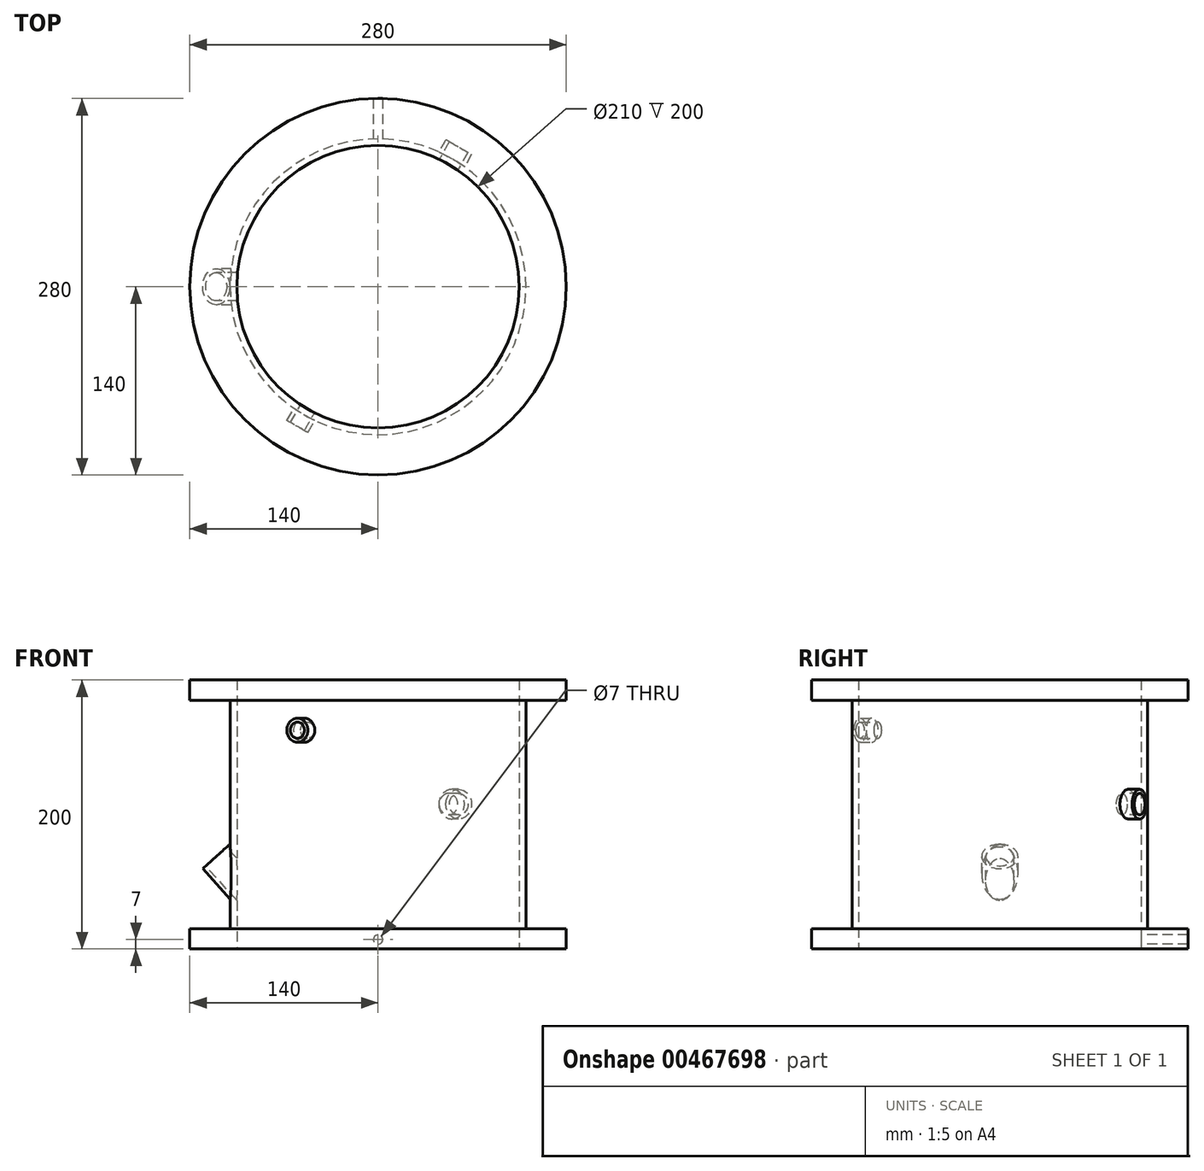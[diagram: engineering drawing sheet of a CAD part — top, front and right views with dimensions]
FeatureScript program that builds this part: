
annotation { "Feature Type Name" : "Feature", "Feature Type Description" : "" }
export const myFeature = defineFeature(function(context is Context, id is Id, definition is map)
    precondition{}
    {
        {
            var Q0;
            Q0=qCreatedBy(makeId("Front.planeOp"),FACE);
            var sketch = newSketch(context, id + "F0", { "sketchPlane" : qUnion([Q0])});
            skLineSegment(sketch, "E0", {"start": v(0, 0) * mm, "end": v(105, 0) * mm, "construction": true});
            skLineSegment(sketch, "E1", {"start": v(105, 0) * mm, "end": v(140, 0) * mm});
            skLineSegment(sketch, "E2", {"start": v(140, 0) * mm, "end": v(140, 15) * mm});
            skLineSegment(sketch, "E3", {"start": v(140, 15) * mm, "end": v(110, 15) * mm});
            skLineSegment(sketch, "E4", {"start": v(110, 15) * mm, "end": v(110, 185) * mm});
            skLineSegment(sketch, "E5", {"start": v(110, 185) * mm, "end": v(140, 185) * mm});
            skLineSegment(sketch, "E6", {"start": v(140, 185) * mm, "end": v(140, 200) * mm});
            skLineSegment(sketch, "E7", {"start": v(140, 200) * mm, "end": v(105, 200) * mm});
            skLineSegment(sketch, "E8", {"start": v(105, 200) * mm, "end": v(105, 0) * mm});
            skLineSegment(sketch, "E9", {"start": v(140, 185) * mm, "end": v(140, 15) * mm, "construction": true});
            skLineSegment(sketch, "E10", {"start": v(0, 0) * mm, "end": v(0, 197.7) * mm, "construction": true});
            skLineSegment(sketch, "E11.bottom", {"start": v(105, 200) * mm, "end": v(85, 200) * mm});
            skLineSegment(sketch, "E11.top", {"start": v(105, 0) * mm, "end": v(85, 0) * mm});
            skLineSegment(sketch, "E11.right", {"start": v(85, 200) * mm, "end": v(85, 0) * mm});
            skSolve(sketch);
        }
        {
            var Q0;
            Q0=makeQuery(id+"F0.imprint","IMPRINT",FACE,{"disambiguationData":[TD([[makeQuery(id+"F0.imprint","IMPRINT",EDGE,{"derivedFrom":sQuery(id+"F0.wireOp",EDGE,"E1")}),1.0]])]});
            var Q1;
            Q1=sQuery(id+"F0.wireOp",EDGE,"E10");
            revolve(context, id + "F1", {"entities" : qUnion([Q0]), "axis" : qUnion([Q1]), "revolveType" : RevolveType.FULL});
        }
        {
            var Q0;
            Q0=qCreatedBy(makeId("Front.planeOp"),FACE);
            var sketch = newSketch(context, id + "F2", { "sketchPlane" : qUnion([Q0])});
            skCircle(sketch, "E12", {"center": v(0, 7) * mm, "radius": 3.5 * mm});
            skSolve(sketch);
        }
        {
            var Q0;
            Q0 = qSketchRegion(id + "F2", true);
            extrude(context, id + "F3", {"entities" : qUnion([Q0]), "operationType" : NewBodyOperationType.REMOVE, "depth" : 150 * mm, "offsetDistance" : 25 * mm});
        }
        {
            var Q0;
            Q0=qCreatedBy(makeId("Front.planeOp"),FACE);
            var sketch = newSketch(context, id + "F4", { "sketchPlane" : qUnion([Q0])});
            skLineSegment(sketch, "E13", {"start": v(0, 77.7) * mm, "end": v(0, 60.53) * mm});
            skLineSegment(sketch, "E14", {"start": v(0, 77.7) * mm, "end": v(-105, 77.7) * mm});
            skLineSegment(sketch, "E15", {"start": v(-105, 77.7) * mm, "end": v(-105, 51.7) * mm});
            skLineSegment(sketch, "E16", {"start": v(-105, 51.7) * mm, "end": v(-120.4, 68.8) * mm});
            skLineSegment(sketch, "E17", {"start": v(-105, 51.7) * mm, "end": v(-105, 49.7) * mm});
            skLineSegment(sketch, "E18", {"start": v(-120.4, 68.8) * mm, "end": v(-110.36, 77.84) * mm});
            skSolve(sketch);
        }
        {
            var Q0;
            Q0=sQuery(id+"F4.wireOp",EDGE,"E18");
            cPlane(context, id + "F5", {"entities" : qUnion([Q0]), "cplaneType" : CPlaneType.LINE_ANGLE, "offset" : 25 * mm, "angle" : 90 * degree, "width" : 150 * mm, "height" : 150 * mm});
        }
        {
            var Q0;
            Q0=qCreatedBy(id+"F5.planeOp",FACE);
            var sketch = newSketch(context, id + "F6", { "sketchPlane" : qUnion([Q0])});
            skCircle(sketch, "E19", {"center": v(-43.43, 0) * mm, "radius": 13.5 * mm});
            skCircle(sketch, "E20.0", {"center": v(-43.43, 0) * mm, "radius": 10.5 * mm});
            skSolve(sketch);
        }
        {
            var Q0;
            Q0=makeQuery(id+"F6.imprint","IMPRINT",FACE,{"disambiguationData":[TD([[makeQuery(id+"F6.imprint","IMPRINT",EDGE,{"derivedFrom":sQuery(id+"F6.wireOp",EDGE,"E19")}),1.0]])]});
            extrude(context, id + "F7", {"entities" : qUnion([Q0]), "operationType" : NewBodyOperationType.ADD, "oppositeDirection" : true, "depth" : 31 * mm});
        }
        {
            var Q0;
            Q0=makeQuery(id+"F0.imprint","IMPRINT",FACE,{"disambiguationData":[TD([[makeQuery(id+"F0.imprint","IMPRINT",EDGE,{"derivedFrom":sQuery(id+"F0.wireOp",EDGE,"E11.bottom")}),1.0]])]});
            var Q1;
            Q1=sQuery(id+"F0.wireOp",EDGE,"E10");
            revolve(context, id + "F8", {"operationType" : NewBodyOperationType.REMOVE, "entities" : qUnion([Q0]), "axis" : qUnion([Q1]), "revolveType" : RevolveType.FULL, "oppositeDirection" : true});
        }
        {
            var Q0;
            Q0=qCreatedBy(makeId("Top.planeOp"),FACE);
            var sketch = newSketch(context, id + "F9", { "sketchPlane" : qUnion([Q0])});
            skLineSegment(sketch, "E21", {"start": v(0, 0) * mm, "end": v(-24.71, 42.8) * mm});
            skLineSegment(sketch, "E22", {"start": v(0, 0) * mm, "end": v(0, 44.2) * mm});
            skSolve(sketch);
        }
        {
            var Q0;
            Q0=sQuery(id+"F9.wireOp",EDGE,"E21");
            cPlane(context, id + "F10", {"entities" : qUnion([Q0]), "cplaneType" : CPlaneType.LINE_ANGLE, "offset" : 25 * mm, "angle" : 90 * degree, "width" : 150 * mm, "height" : 150 * mm});
        }
        {
            var Q0;
            Q0=qCreatedBy(id+"F10.planeOp",FACE);
            var sketch = newSketch(context, id + "F11", { "sketchPlane" : qUnion([Q0])});
            skLineSegment(sketch, "E23", {"start": v(0, 162.7) * mm, "end": v(105, 162.7) * mm});
            skLineSegment(sketch, "E24", {"start": v(105, 162.7) * mm, "end": v(120, 162.7) * mm});
            skLineSegment(sketch, "E25", {"start": v(0, 107.7) * mm, "end": v(-105, 107.7) * mm});
            skLineSegment(sketch, "E26", {"start": v(-105, 107.7) * mm, "end": v(-120, 107.7) * mm});
            skLineSegment(sketch, "E27", {"start": v(-105, 107.7) * mm, "end": v(-105, 118.7) * mm});
            skLineSegment(sketch, "E28", {"start": v(-105, 118.7) * mm, "end": v(-120, 118.7) * mm});
            skLineSegment(sketch, "E29", {"start": v(-120, 118.7) * mm, "end": v(-120, 115.7) * mm});
            skLineSegment(sketch, "E30", {"start": v(-120, 115.7) * mm, "end": v(-105, 115.7) * mm});
            skLineSegment(sketch, "E31", {"start": v(105, 162.7) * mm, "end": v(105, 171.7) * mm});
            skLineSegment(sketch, "E32", {"start": v(105, 171.7) * mm, "end": v(120, 171.7) * mm});
            skLineSegment(sketch, "E33", {"start": v(120, 171.7) * mm, "end": v(120, 168.7) * mm});
            skLineSegment(sketch, "E34", {"start": v(120, 168.7) * mm, "end": v(105, 168.7) * mm});
            skLineSegment(sketch, "E35.bottom", {"start": v(-98.9, 115.7) * mm, "end": v(-124.7, 115.7) * mm});
            skLineSegment(sketch, "E35.top", {"start": v(-98.9, 107.7) * mm, "end": v(-124.7, 107.7) * mm});
            skLineSegment(sketch, "E35.left", {"start": v(-98.9, 115.7) * mm, "end": v(-98.9, 107.7) * mm});
            skLineSegment(sketch, "E35.right", {"start": v(-124.7, 115.7) * mm, "end": v(-124.7, 107.7) * mm});
            skSolve(sketch);
        }
        {
            var Q0;
            {var subQ0=sQuery(id+"F11.wireOp",EDGE,"E32");Q0=makeQuery(id+"F11.imprint","IMPRINT",FACE,{"disambiguationData":[TD([[makeQuery(id+"F11.imprint","IMPRINT",EDGE,{"derivedFrom":subQ0}),-1.0]])]});}
            var Q1;
            Q1=sQuery(id+"F11.wireOp",EDGE,"E24");
            revolve(context, id + "F12", {"operationType" : NewBodyOperationType.ADD, "entities" : qUnion([Q0]), "axis" : qUnion([Q1]), "revolveType" : RevolveType.FULL});
        }
        {
            var Q0;
            {var subQ0=sQuery(id+"F11.wireOp",EDGE,"E28");Q0=makeQuery(id+"F11.imprint","IMPRINT",FACE,{"disambiguationData":[TD([[makeQuery(id+"F11.imprint","IMPRINT",EDGE,{"derivedFrom":subQ0}),1.0]])]});}
            var Q1;
            Q1=sQuery(id+"F11.wireOp",EDGE,"E26");
            revolve(context, id + "F13", {"operationType" : NewBodyOperationType.ADD, "entities" : qUnion([Q0]), "axis" : qUnion([Q1]), "revolveType" : RevolveType.FULL});
        }
        {
            var Q0;
            Q0=makeQuery(id+"F6.imprint","IMPRINT",FACE,{"disambiguationData":[TD([[makeQuery(id+"F6.imprint","IMPRINT",EDGE,{"derivedFrom":sQuery(id+"F6.wireOp",EDGE,"E20.0")}),1.0]])]});
            extrude(context, id + "F14", {"entities" : qUnion([Q0]), "operationType" : NewBodyOperationType.REMOVE, "oppositeDirection" : true, "depth" : 4000 * mm, "offsetDistance" : 25 * mm});
        }
        {
            var Q0;
            Q0=makeQuery(id+"F13.opRevolve","SWEPT_FACE",FACE,{"disambiguationData":[OSD([sQuery(id+"F11.wireOp",EDGE,"E29")])]});
            var sketch = newSketch(context, id + "F15", { "sketchPlane" : qUnion([Q0])});
            skCircle(sketch, "E36", {"center": v(0, 107.7) * mm, "radius": 8 * mm});
            skPoint(sketch, "E36.first.point", {"position": v(-7.9, 108.91) * mm});
            skPoint(sketch, "E36.second.point", {"position": v(3.04, 115.11) * mm});
            skPoint(sketch, "E36.third.point", {"position": v(4.75, 101.28) * mm});
            skSolve(sketch);
        }
        {
            var Q0;
            Q0=makeQuery(id+"F15.imprint","IMPRINT",FACE,{"disambiguationData":[TD([[makeQuery(id+"F15.imprint","IMPRINT",EDGE,{"derivedFrom":sQuery(id+"F15.wireOp",EDGE,"E36")}),-1.0]])]});
            extrude(context, id + "F16", {"entities" : qUnion([Q0]), "operationType" : NewBodyOperationType.REMOVE, "oppositeDirection" : true, "depth" : 25 * mm, "offsetDistance" : 25 * mm});
        }
        {
            var Q0;
            Q0=makeQuery(id+"F12.opRevolve","SWEPT_FACE",FACE,{"disambiguationData":[OSD([sQuery(id+"F11.wireOp",EDGE,"E33")])]});
            var sketch = newSketch(context, id + "F17", { "sketchPlane" : qUnion([Q0])});
            skCircle(sketch, "E37", {"center": v(0, 162.7) * mm, "radius": 6 * mm});
            skPoint(sketch, "E37.first.point", {"position": v(-5.95, 163.5) * mm});
            skPoint(sketch, "E37.second.point", {"position": v(2.1, 157.09) * mm});
            skPoint(sketch, "E37.third.point", {"position": v(3.59, 167.52) * mm});
            skSolve(sketch);
        }
        {
            var Q0;
            Q0 = qSketchRegion(id + "F17", true);
            extrude(context, id + "F18", {"entities" : qUnion([Q0]), "operationType" : NewBodyOperationType.REMOVE, "oppositeDirection" : true, "depth" : 25 * mm, "offsetDistance" : 25 * mm});
        }
        {
            var Q0;
            Q0=sQuery(id+"F4.wireOp",EDGE,"E18");
            cPlane(context, id + "F19", {"entities" : qUnion([Q0]), "cplaneType" : CPlaneType.LINE_ANGLE, "offset" : 25 * mm, "angle" : 0 * degree, "width" : 150 * mm, "height" : 150 * mm});
        }
        {
            var Q0;
            Q0=makeQuery(id+"F1.opRevolve","SWEPT_BODY",BODY,{"disambiguationData":[OSD([sQuery(id+"F0.wireOp",EDGE,"E1"),sQuery(id+"F0.wireOp",EDGE,"E2"),sQuery(id+"F0.wireOp",EDGE,"E3"),sQuery(id+"F0.wireOp",EDGE,"E4"),sQuery(id+"F0.wireOp",EDGE,"E5"),sQuery(id+"F0.wireOp",EDGE,"E6"),sQuery(id+"F0.wireOp",EDGE,"E7"),sQuery(id+"F0.wireOp",EDGE,"E8")])]});
            var Q1;
            Q1=qCreatedBy(id+"F19.planeOp",FACE);
            mirror(context, id + "F20", {"entities" : qUnion([Q0]), "mirrorPlane" : qUnion([Q1])});
        }
        {
            var Q0;
            Q0=makeQuery(id+"F1.opRevolve","SWEPT_BODY",BODY,{"disambiguationData":[OSD([sQuery(id+"F0.wireOp",EDGE,"E1"),sQuery(id+"F0.wireOp",EDGE,"E2"),sQuery(id+"F0.wireOp",EDGE,"E3"),sQuery(id+"F0.wireOp",EDGE,"E4"),sQuery(id+"F0.wireOp",EDGE,"E5"),sQuery(id+"F0.wireOp",EDGE,"E6"),sQuery(id+"F0.wireOp",EDGE,"E7"),sQuery(id+"F0.wireOp",EDGE,"E8")])]});
            deleteBodies(context, id + "F21", {"entities" : qUnion([Q0])});
        }
    });
